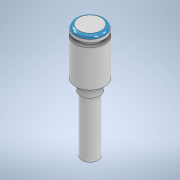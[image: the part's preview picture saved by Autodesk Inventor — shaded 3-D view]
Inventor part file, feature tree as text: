
AUTODESK INVENTOR PART (.ipt)
format: ipt  version: 2021 (Build 250183000, 183)  size: 136,192 bytes
history: native  units: mm
features: extrude x5, sketch x5, fillet x1
ambient origin geometry x8: Origin, YZ Plane, XZ Plane, XY Plane, X Axis, Y Axis, Z Axis, Center Point
bodies: Solid1 (feature_tree)
feature tree (11):
  extrude  "Extrusion1"  Depth=14.2mm TaperAngle=0.0deg
  extrude  "Extrusion2"  Depth=2.7mm TaperAngle=0.0deg
  extrude  "Extrusion3"  Depth=9.2mm TaperAngle=0.0deg
  extrude  "Extrusion4"  Depth=1.0mm TaperAngle=0.0deg
  extrude  "Extrusion5"  Depth=1.5mm TaperAngle=0.0deg
  fillet  "Fillet1"  Radius=0.8mm
  sketch  "Sketch1"  dims[d0=4.0mm d1=14.2mm d2=0.0mm]
  sketch  "Sketch2"  dims[d3=4.8mm d4=2.7mm d5=0.0mm]
  sketch  "Sketch3"  dims[d6=7.4mm d7=9.2mm d8=0.0mm]
  sketch  "Sketch4"  dims[d9=5.5mm d10=1.0mm d11=0.0mm]
  sketch  "Sketch5"  dims[d12=7.2mm d13=1.5mm d14=0.0mm d15=0.8mm]
